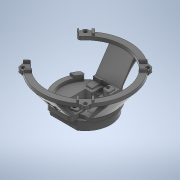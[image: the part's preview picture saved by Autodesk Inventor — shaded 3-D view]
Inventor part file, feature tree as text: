
AUTODESK INVENTOR PART (.ipt)
format: ipt  version: 2020 (Build 240168000, 168)  size: 1,585,152 bytes
history: native  units: mm
features: projected_geometry x56, sketch x33, extrude x26, other x10, fillet x9, chamfer x4, loft x2, mirror x2, revolve x1, pattern_circular x1
ambient origin geometry x8: Origin, YZ Plane, XZ Plane, XY Plane, X Axis, Y Axis, Z Axis, Center Point
bodies: Body1 (feature_tree)
feature tree (144):
  other  "Твердое тело1"
  extrude  "Выдавливание1"  Depth=17.1mm
  extrude  "Выдавливание2"  Depth=17.1mm
  other  "РабПлоскость1"
  sketch  "Эскиз3"
  other  "РабОсь1"
  revolve  "Вращение1"
  extrude  "Выдавливание3"  Depth=25.0mm
  extrude  "Выдавливание4"  Depth=5.3mm
  extrude  "Выдавливание5"  Depth=44.7mm
  extrude  "Выдавливание6"  Depth=7.7mm TaperAngle=0.0deg
  extrude  "Выдавливание7"  Depth=5.0mm
  extrude  "Выдавливание8"  Depth=30.65mm
  sketch  "Эскиз10"
  extrude  "Выдавливание9"  Depth=2.5mm TaperAngle=0.0deg
  fillet  "Сопряжение1"  Radius=0.2mm
  fillet  "Сопряжение2"  [1 undecoded]
  fillet  "Сопряжение3"  Radius=1.85mm
  extrude  "Выдавливание10"  Depth=30.0mm
  fillet  "Сопряжение4"  Radius=2.0mm
  fillet  "Сопряжение5"  Radius=3.0mm
  extrude  "камера"  Depth=38.0mm
  extrude  "труба"  Depth=10.0mm TaperAngle=0.0deg
  sketch  "Эскиз15"
  other  "РабПлоскость2"
  extrude  "Выдавливание12"  Depth=5.2mm
  extrude  "Выдавливание13"  Depth=6.2mm
  chamfer  "Фаска1"  Distance=29.46mm
  fillet  "Сопряжение6"  Radius=10.0mm
  fillet  "Сопряжение7"  Radius=9.5mm
  other  "РабОсь2"
  pattern_circular  "Круговой массив1"  [2 undecoded]
  extrude  "Выдавливание15"  TaperAngle=60.0deg  [1 undecoded]
  chamfer  "Фаска2"  Distance=6.0mm
  sketch  "Эскиз20"
  extrude  "Выдавливание16"  Depth=6.0mm
  fillet  "Сопряжение8"  Radius=14.2mm
  other  "РабПлоскость3"
  extrude  "Выдавливание17"  Depth=9.5mm
  extrude  "Выдавливание18"  Depth=2.0mm
  sketch  "Эскиз24"
  sketch  "Эскиз25"
  sketch  "Эскиз26"
  extrude  "Выдавливание19"  Depth=13.962634mm
  loft  "Лофт1"
  other  "РабПлоскость4"
  mirror  "Зеркальное отражение1"
  extrude  "Выдавливание20"  Depth=2.0mm TaperAngle=0.0deg
  loft  "Лофт2"
  extrude  "Выдавливание21"  Depth=6.2mm
  chamfer  "Фаска3"  Distance=6.0mm
  chamfer  "Фаска4"  Distance=1.7mm
  extrude  "Выдавливание22"  Depth=1.5mm TaperAngle=0.0deg
  extrude  "Выдавливание23"  Depth=6.0mm TaperAngle=0.0deg
  fillet  "Сопряжение9"  Radius=0.5mm
  extrude  "Выдавливание24"  Depth=0.7mm
  extrude  "Выдавливание25"  Depth=1.0mm
  other  "РабПлоскость5"
  extrude  "Выдавливание26"  Depth=6.0mm TaperAngle=0.0deg
  mirror  "Зеркальное отражение2"
  sketch  "Эскиз1"
  sketch  "Эскиз2"
  projected_geometry  "Спроецированная петля1"
  projected_geometry  "Спроецированная петля2"
  sketch  "Эскиз4"
  projected_geometry  "Спроецированная петля3"
  sketch  "Эскиз5"
  sketch  "Эскиз6"
  projected_geometry  "Спроецированная петля4"
  sketch  "Эскиз7"
  projected_geometry  "Спроецированная петля5"
  sketch  "Эскиз8"
  projected_geometry  "Спроецированная петля6"
  projected_geometry  "Спроецированная петля7"
  projected_geometry  "Спроецированная петля8"
  sketch  "Эскиз9"
  projected_geometry  "Спроецированная петля9"
  projected_geometry  "Спроецированная петля10"
  projected_geometry  "Спроецированная петля11"
  projected_geometry  "Спроецированная петля12"
  sketch  "Эскиз11"
  sketch  "Эскиз12"
  projected_geometry  "Спроецированная петля13"
  projected_geometry  "Спроецированная петля14"
  projected_geometry  "Спроецированная петля15"
  sketch  "Эскиз14"
  projected_geometry  "Спроецированная петля20"
  projected_geometry  "Спроецированная петля21"
  projected_geometry  "Спроецированная петля22"
  projected_geometry  "Спроецированная петля23"
  sketch  "Эскиз16"
  projected_geometry  "Спроецированная петля24"
  sketch  "Эскиз17"
  projected_geometry  "Спроецированная петля25"
  sketch  "Эскиз18"
  sketch  "Эскиз19"
  projected_geometry  "Спроецированная петля26"
  projected_geometry  "Спроецированная петля27"
  projected_geometry  "Спроецированная петля28"
  projected_geometry  "Спроецированная петля29"
  sketch  "Эскиз21"
  projected_geometry  "Спроецированная петля30"
  projected_geometry  "Спроецированная петля31"
  projected_geometry  "Спроецированная петля32"
  projected_geometry  "Спроецированная петля33"
  projected_geometry  "Спроецированная петля34"
  projected_geometry  "Спроецированная петля35"
  projected_geometry  "Спроецированная петля36"
  projected_geometry  "Спроецированная петля37"
  projected_geometry  "Спроецированная петля38"
  projected_geometry  "Спроецированная петля39"
  sketch  "Эскиз22"
  projected_geometry  "Спроецированная петля40"
  projected_geometry  "Спроецированная петля41"
  projected_geometry  "Спроецированная петля42"
  projected_geometry  "Спроецированная петля43"
  projected_geometry  "Спроецированная петля44"
  sketch  "Эскиз23"
  projected_geometry  "Спроецированная петля45"
  projected_geometry  "Спроецированная петля46"
  projected_geometry  "Спроецированная петля47"
  projected_geometry  "Спроецированная петля48"
  projected_geometry  "Спроецированная петля49"
  projected_geometry  "Спроецированная петля50"
  other  "Ребра1"
  sketch  "Эскиз27"
  projected_geometry  "Спроецированная петля51"
  sketch  "Эскиз28"
  projected_geometry  "Спроецированная петля52"
  projected_geometry  "Спроецированная петля53"
  other  "Ребра2"
  sketch  "Эскиз31"
  sketch  "Эскиз32"
  projected_geometry  "Спроецированная петля54"
  projected_geometry  "Спроецированная петля55"
  sketch  "Эскиз33"
  projected_geometry  "Спроецированная петля56"
  sketch  "Эскиз34"
  sketch  "Эскиз35"
  projected_geometry  "Спроецированная петля57"
  sketch  "Эскиз36"
  projected_geometry  "Спроецированная петля58"
  projected_geometry  "Спроецированная петля59"
  projected_geometry  "Спроецированная петля60"
note: 4 required parameter values undecoded (feature->parameter linkage not recoverable at this tier; creation-order binding heuristic only, values carry confidence <= 0.55)
